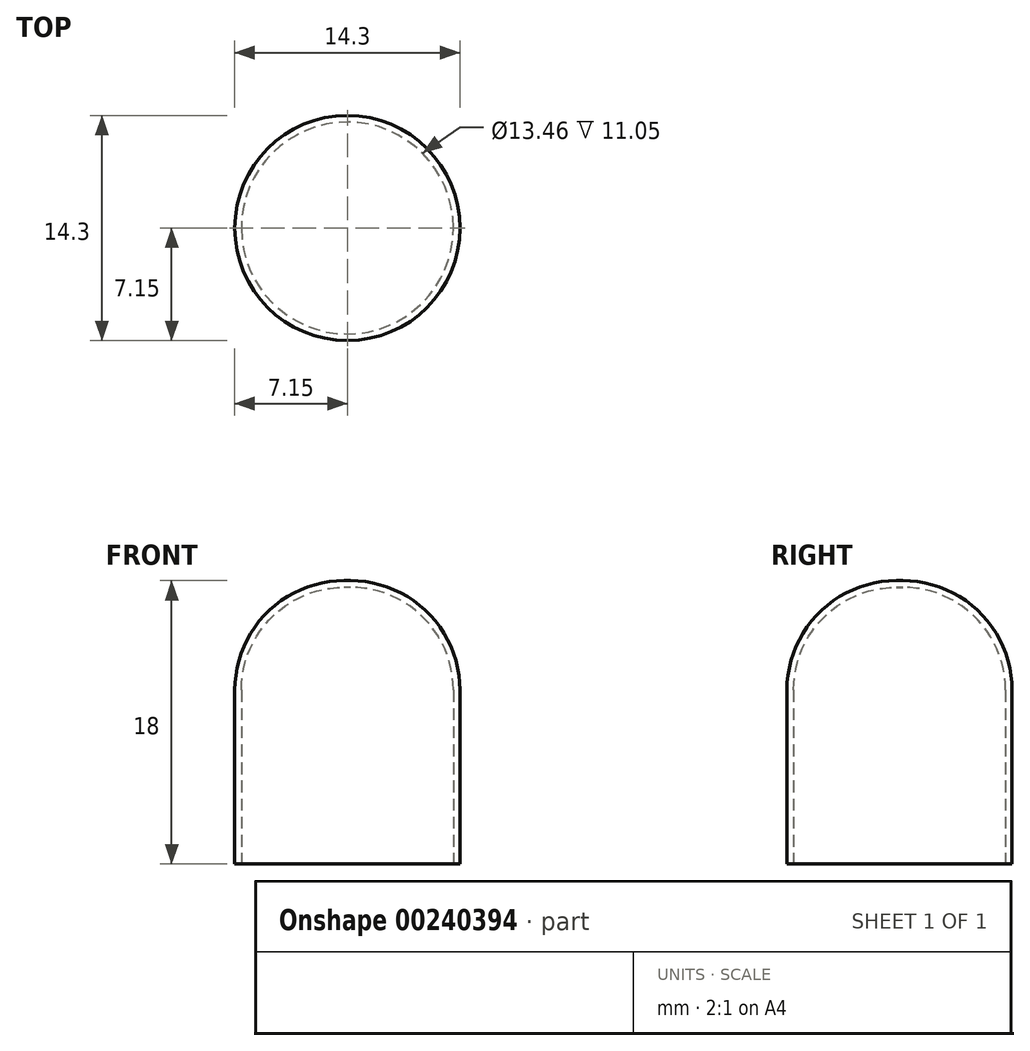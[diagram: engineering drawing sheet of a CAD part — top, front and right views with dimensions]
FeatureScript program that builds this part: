
annotation { "Feature Type Name" : "Feature", "Feature Type Description" : "" }
export const myFeature = defineFeature(function(context is Context, id is Id, definition is map)
    precondition{}
    {
        {
            var Q0;
            Q0=qCreatedBy(makeId("Top.planeOp"),FACE);
            var sketch = newSketch(context, id + "F0", { "sketchPlane" : qUnion([Q0])});
            skCircle(sketch, "E0", {"center": v(0, 0) * mm, "radius": 6.75 * mm});
            skCircle(sketch, "E1", {"center": v(0, 0) * mm, "radius": 7.15 * mm});
            skSolve(sketch);
        }
        {
            var Q0;
            Q0 = qSketchRegion(id + "F0", true);
            var Q1;
            Q1=makeQuery(id+"F0.imprint","IMPRINT",FACE,{"disambiguationData":[TD([[makeQuery(id+"F0.imprint","IMPRINT",EDGE,{"derivedFrom":sQuery(id+"F0.wireOp",EDGE,"E0")}),1.0]])]});
            extrude(context, id + "F1", {"entities" : qUnion([Q0, Q1]), "depth" : 18 * mm});
        }
        {
            var Q0;
            Q0=makeQuery(id+"F1.opExtrude","CAP_EDGE",EDGE,{"disambiguationData":[OSD([sQuery(id+"F0.wireOp",EDGE,"E1")])],"isStart":false});
            fillet(context, id + "F2", {"entities" : qUnion([Q0]), "radius" : 6.95 * mm, "tangentPropagation" : true, "allowEdgeOverflow" : false});
        }
        {
            var Q0;
            Q0=makeQuery(id+"F1.opExtrude","CAP_FACE",FACE,{"disambiguationData":[OSD([sQuery(id+"F0.wireOp",EDGE,"E1")])],"isStart":true});
            shell(context, id + "F3", {"entities" : qUnion([Q0]), "thickness" : 0.42 * mm});
        }
    });
